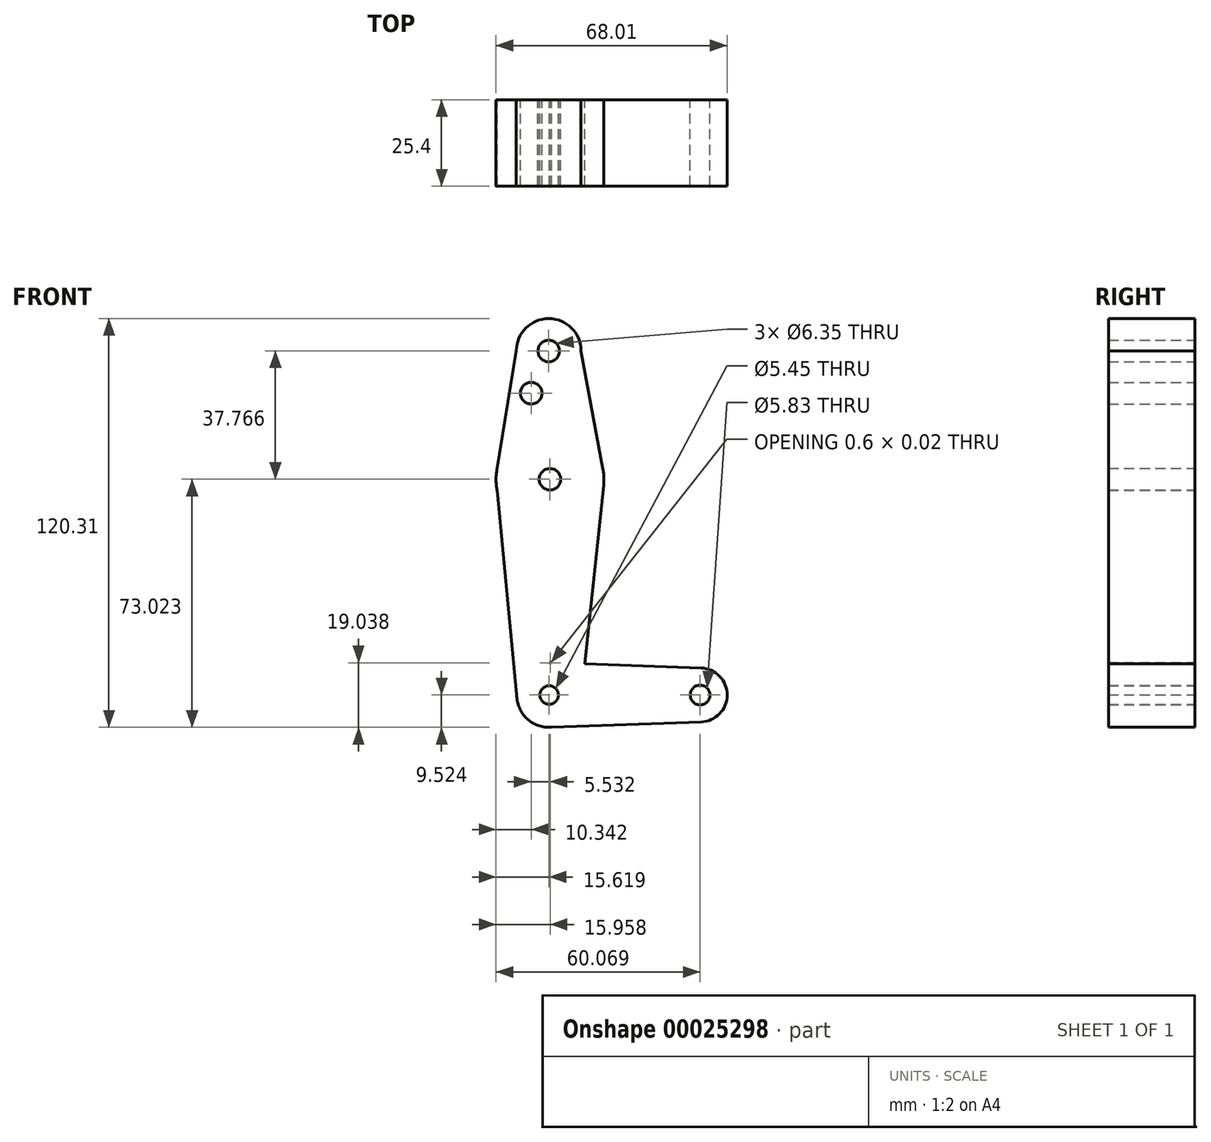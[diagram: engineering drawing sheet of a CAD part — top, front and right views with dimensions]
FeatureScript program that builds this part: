
annotation { "Feature Type Name" : "Feature", "Feature Type Description" : "" }
export const myFeature = defineFeature(function(context is Context, id is Id, definition is map)
    precondition{}
    {
        {
            var Q0;
            Q0=qCreatedBy(makeId("Front.planeOp"),FACE);
            var sketch = newSketch(context, id + "F0", { "sketchPlane" : qUnion([Q0])});
            skCircle(sketch, "E0", {"center": v(-58.84, 57.39) * mm, "radius": 9.53 * mm});
            skCircle(sketch, "E1", {"center": v(-58.48, 19.62) * mm, "radius": 15.88 * mm});
            skCircle(sketch, "E2", {"center": v(-58.73, -43.88) * mm, "radius": 9.53 * mm});
            skCircle(sketch, "E3", {"center": v(-14.28, -43.88) * mm, "radius": 7.94 * mm});
            skLineSegment(sketch, "E4", {"start": v(-58.84, 57.39) * mm, "end": v(-58.48, 19.62) * mm});
            skLineSegment(sketch, "E5", {"start": v(-58.48, 19.62) * mm, "end": v(-58.73, -43.88) * mm});
            skLineSegment(sketch, "E6", {"start": v(-58.73, -43.88) * mm, "end": v(-14.28, -43.88) * mm});
            skLineSegment(sketch, "E7", {"start": v(-58.7, -34.35) * mm, "end": v(-14, -35.94) * mm});
            skLineSegment(sketch, "E8", {"start": v(-58.04, -53.38) * mm, "end": v(-14, -51.8) * mm});
            skLineSegment(sketch, "E9", {"start": v(-68.37, 57.39) * mm, "end": v(-74.14, 22.2) * mm});
            skLineSegment(sketch, "E10", {"start": v(-49.32, 57.39) * mm, "end": v(-42.87, 22.51) * mm});
            skLineSegment(sketch, "E11", {"start": v(-68.26, -43.88) * mm, "end": v(-74.35, 19.84) * mm});
            skLineSegment(sketch, "E12", {"start": v(-49.2, -43.88) * mm, "end": v(-42.5, 19.84) * mm});
            skCircle(sketch, "E13", {"center": v(-64, 44.98) * mm, "radius": 3.18 * mm});
            skCircle(sketch, "E14", {"center": v(-58.73, -43.88) * mm, "radius": 2.73 * mm});
            skCircle(sketch, "E15", {"center": v(-58.84, 57.39) * mm, "radius": 3.18 * mm});
            skCircle(sketch, "E16", {"center": v(-58.48, 19.62) * mm, "radius": 3.18 * mm});
            skCircle(sketch, "E17", {"center": v(-14.28, -43.88) * mm, "radius": 2.91 * mm});
            skSolve(sketch);
        }
        {
            var Q0;
            {var subQ0=sQuery(id+"F0.wireOp",EDGE,"E11");var subQ1=sQuery(id+"F0.wireOp",EDGE,"E1");var subQ3=makeQuery(id+"F0.imprint","INTERSECT",VERTEX,{"disambiguationData":[OD(0.0)],"derivedFrom":[subQ1,subQ0]});Q0=makeQuery(id+"F0.imprint","IMPRINT",FACE,{"disambiguationData":[TD([[makeQuery(id+"F0.imprint","IMPRINT",EDGE,{"disambiguationData":[TD([[subQ3,-1.0]])],"derivedFrom":subQ1}),1.0]])]});}
            var Q1;
            {var subQ0=sQuery(id+"F0.wireOp",EDGE,"E0");var subQ3=makeQuery(id+"F0.imprint","INTERSECT",VERTEX,{"derivedFrom":[subQ0,sQuery(id+"F0.wireOp",EDGE,"E9")]});Q1=makeQuery(id+"F0.imprint","IMPRINT",FACE,{"disambiguationData":[TD([[makeQuery(id+"F0.imprint","IMPRINT",EDGE,{"disambiguationData":[TD([[subQ3,1.0]])],"derivedFrom":subQ0}),1.0]])]});}
            var Q2;
            {var subQ0=sQuery(id+"F0.wireOp",EDGE,"E9");Q2=makeQuery(id+"F0.imprint","IMPRINT",FACE,{"disambiguationData":[TD([[makeQuery(id+"F0.imprint","IMPRINT",EDGE,{"derivedFrom":subQ0}),1.0]])]});}
            var Q3;
            {var subQ0=sQuery(id+"F0.wireOp",EDGE,"E10");Q3=makeQuery(id+"F0.imprint","IMPRINT",FACE,{"disambiguationData":[TD([[makeQuery(id+"F0.imprint","IMPRINT",EDGE,{"derivedFrom":subQ0}),-1.0]])]});}
            var Q4;
            {var subQ1=sQuery(id+"F0.wireOp",EDGE,"E1");var subQ6=makeQuery(id+"F0.imprint","INTERSECT",VERTEX,{"derivedFrom":[subQ1,sQuery(id+"F0.wireOp",EDGE,"E10")]});Q4=makeQuery(id+"F0.imprint","IMPRINT",FACE,{"disambiguationData":[TD([[makeQuery(id+"F0.imprint","IMPRINT",EDGE,{"disambiguationData":[TD([[subQ6,-1.0]])],"derivedFrom":subQ1}),1.0]])]});}
            var Q5;
            {var subQ0=sQuery(id+"F0.wireOp",EDGE,"E11");var subQ1=sQuery(id+"F0.wireOp",EDGE,"E1");var subQ2=makeQuery(id+"F0.imprint","INTERSECT",VERTEX,{"disambiguationData":[OD(1.0)],"derivedFrom":[subQ1,subQ0]});Q5=makeQuery(id+"F0.imprint","IMPRINT",FACE,{"disambiguationData":[TD([[makeQuery(id+"F0.imprint","IMPRINT",EDGE,{"disambiguationData":[TD([[subQ2,-1.0]])],"derivedFrom":subQ1}),-1.0]])]});}
            var Q6;
            {var subQ1=sQuery(id+"F0.wireOp",EDGE,"E2");var subQ6=makeQuery(id+"F0.imprint","INTERSECT",VERTEX,{"derivedFrom":[subQ1,sQuery(id+"F0.wireOp",EDGE,"E8")]});Q6=makeQuery(id+"F0.imprint","IMPRINT",FACE,{"disambiguationData":[TD([[makeQuery(id+"F0.imprint","IMPRINT",EDGE,{"disambiguationData":[TD([[subQ6,1.0]])],"derivedFrom":subQ1}),1.0]])]});}
            var Q7;
            {var subQ0=sQuery(id+"F0.wireOp",EDGE,"E8");Q7=makeQuery(id+"F0.imprint","IMPRINT",FACE,{"disambiguationData":[TD([[makeQuery(id+"F0.imprint","IMPRINT",EDGE,{"derivedFrom":subQ0}),1.0]])]});}
            var Q8;
            {var subQ1=sQuery(id+"F0.wireOp",EDGE,"E7");var subQ5=sQuery(id+"F0.wireOp",EDGE,"E3");var subQ6=makeQuery(id+"F0.imprint","INTERSECT",VERTEX,{"derivedFrom":[subQ5,subQ1]});Q8=makeQuery(id+"F0.imprint","IMPRINT",FACE,{"disambiguationData":[TD([[makeQuery(id+"F0.imprint","IMPRINT",EDGE,{"disambiguationData":[TD([[subQ6,-1.0]])],"derivedFrom":subQ5}),-1.0]])]});}
            var Q9;
            {var subQ1=sQuery(id+"F0.wireOp",EDGE,"E1");var subQ9=makeQuery(id+"F0.imprint","INTERSECT",VERTEX,{"derivedFrom":[subQ1,sQuery(id+"F0.wireOp",EDGE,"E9")]});Q9=makeQuery(id+"F0.imprint","IMPRINT",FACE,{"disambiguationData":[TD([[makeQuery(id+"F0.imprint","IMPRINT",EDGE,{"disambiguationData":[TD([[subQ9,1.0]])],"derivedFrom":subQ1}),1.0]])]});}
            var Q10;
            {var subQ3=sQuery(id+"F0.wireOp",EDGE,"E12");var subQ6=sQuery(id+"F0.wireOp",EDGE,"E1");var subQ9=makeQuery(id+"F0.imprint","INTERSECT",VERTEX,{"derivedFrom":[subQ6,subQ3]});Q10=makeQuery(id+"F0.imprint","IMPRINT",FACE,{"disambiguationData":[TD([[makeQuery(id+"F0.imprint","IMPRINT",EDGE,{"disambiguationData":[TD([[subQ9,1.0]])],"derivedFrom":subQ6}),-1.0]])]});}
            var Q11;
            {var subQ0=sQuery(id+"F0.wireOp",EDGE,"E7");var subQ1=sQuery(id+"F0.wireOp",EDGE,"E2");var subQ2=makeQuery(id+"F0.imprint","INTERSECT",VERTEX,{"derivedFrom":[subQ1,subQ0]});Q11=makeQuery(id+"F0.imprint","IMPRINT",FACE,{"disambiguationData":[TD([[makeQuery(id+"F0.imprint","IMPRINT",EDGE,{"disambiguationData":[TD([[subQ2,1.0]])],"derivedFrom":subQ1}),1.0]])]});}
            var Q12;
            {var subQ0=sQuery(id+"F0.wireOp",EDGE,"E12");var subQ1=sQuery(id+"F0.wireOp",EDGE,"E7");var subQ2=makeQuery(id+"F0.imprint","INTERSECT",VERTEX,{"derivedFrom":[subQ1,subQ0]});Q12=makeQuery(id+"F0.imprint","IMPRINT",FACE,{"disambiguationData":[TD([[makeQuery(id+"F0.imprint","IMPRINT",EDGE,{"disambiguationData":[TD([[subQ2,1.0]])],"derivedFrom":subQ1}),-1.0]])]});}
            var Q13;
            {var subQ0=sQuery(id+"F0.wireOp",EDGE,"E3");var subQ2=makeQuery(id+"F0.imprint","INTERSECT",VERTEX,{"derivedFrom":[subQ0,sQuery(id+"F0.wireOp",EDGE,"E7")]});Q13=makeQuery(id+"F0.imprint","IMPRINT",FACE,{"disambiguationData":[TD([[makeQuery(id+"F0.imprint","IMPRINT",EDGE,{"disambiguationData":[TD([[subQ2,-1.0]])],"derivedFrom":subQ0}),1.0]])]});}
            extrude(context, id + "F1", {"entities" : qUnion([Q0, Q1, Q2, Q3, Q4, Q5, Q6, Q7, Q8, Q9, Q10, Q11, Q12, Q13]), "depth" : 25.4 * mm});
        }
    });
